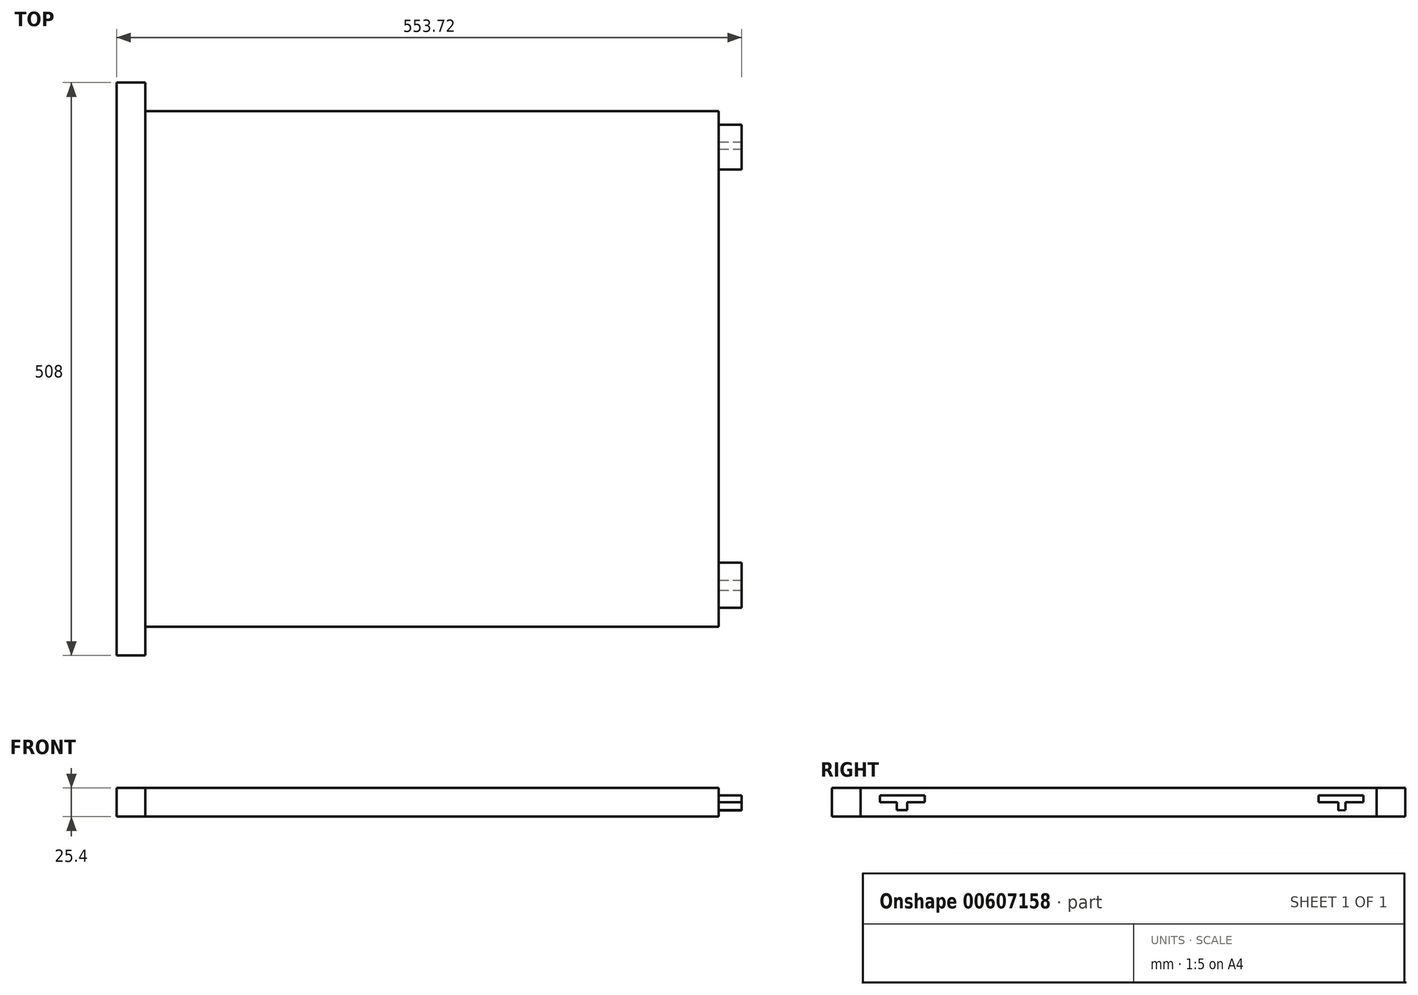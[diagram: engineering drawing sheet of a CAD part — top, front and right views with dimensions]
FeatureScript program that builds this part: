
annotation { "Feature Type Name" : "Feature", "Feature Type Description" : "" }
export const myFeature = defineFeature(function(context is Context, id is Id, definition is map)
    precondition{}
    {
        {
            var Q0;
            Q0=qCreatedBy(makeId("Top.planeOp"),FACE);
            var sketch = newSketch(context, id + "F0", { "sketchPlane" : qUnion([Q0])});
            skLineSegment(sketch, "E0.bottom", {"start": v(-230.83, 140.76) * mm, "end": v(277.17, 140.76) * mm});
            skLineSegment(sketch, "E0.top", {"start": v(-230.83, -316.44) * mm, "end": v(277.17, -316.44) * mm});
            skLineSegment(sketch, "E0.left", {"start": v(-230.83, 140.76) * mm, "end": v(-230.83, -316.44) * mm});
            skLineSegment(sketch, "E0.right", {"start": v(277.17, 140.76) * mm, "end": v(277.17, -316.44) * mm});
            skSolve(sketch);
        }
        {
            var Q0;
            Q0=makeQuery(id+"F0.imprint","IMPRINT",FACE,{"disambiguationData":[TD([[makeQuery(id+"F0.imprint","IMPRINT",EDGE,{"derivedFrom":sQuery(id+"F0.wireOp",EDGE,"E0.bottom")}),-1.0]])]});
            extrude(context, id + "F1", {"entities" : qUnion([Q0]), "depth" : 25.4 * mm, "offsetDistance" : 25.4 * mm});
        }
        {
            var Q0;
            Q0=makeQuery(id+"F1.opExtrude","CAP_FACE",FACE,{"disambiguationData":[OSD([sQuery(id+"F0.wireOp",EDGE,"E0.bottom"),sQuery(id+"F0.wireOp",EDGE,"E0.top"),sQuery(id+"F0.wireOp",EDGE,"E0.left"),sQuery(id+"F0.wireOp",EDGE,"E0.right")])],"isStart":true});
            var sketch = newSketch(context, id + "F2", { "sketchPlane" : qUnion([Q0])});
            skLineSegment(sketch, "E1.bottom", {"start": v(-230.83, 341.84) * mm, "end": v(-256.23, 341.84) * mm});
            skLineSegment(sketch, "E1.top", {"start": v(-230.83, -166.16) * mm, "end": v(-256.23, -166.16) * mm});
            skLineSegment(sketch, "E1.left", {"start": v(-230.83, 341.84) * mm, "end": v(-230.83, -166.16) * mm});
            skLineSegment(sketch, "E1.right", {"start": v(-256.23, 341.84) * mm, "end": v(-256.23, -166.16) * mm});
            skSolve(sketch);
        }
        {
            var Q0;
            {var subQ2=sQuery(id+"F2.wireOp",EDGE,"E1.bottom");Q0=makeQuery(id+"F2.imprint","IMPRINT",FACE,{"disambiguationData":[TD([[makeQuery(id+"F2.imprint","IMPRINT",EDGE,{"derivedFrom":subQ2}),1.0]])]});}
            var Q1;
            Q1=makeQuery(id+"F1.opExtrude","CAP_FACE",FACE,{"disambiguationData":[OSD([sQuery(id+"F0.wireOp",EDGE,"E0.bottom"),sQuery(id+"F0.wireOp",EDGE,"E0.top"),sQuery(id+"F0.wireOp",EDGE,"E0.left"),sQuery(id+"F0.wireOp",EDGE,"E0.right")])],"isStart":false});
            extrude(context, id + "F3", {"entities" : qUnion([Q0]), "endBound" : BoundingType.UP_TO_SURFACE, "oppositeDirection" : true, "depth" : 76.2 * mm, "endBoundEntityFace" : qUnion([Q1]), "offsetDistance" : 25.4 * mm});
        }
        {
            var Q0;
            Q0=makeQuery(id+"F1.opExtrude","SWEPT_FACE",FACE,{"disambiguationData":[OSD([sQuery(id+"F0.wireOp",EDGE,"E0.right")])]});
            var sketch = newSketch(context, id + "F4", { "sketchPlane" : qUnion([Q0])});
            skLineSegment(sketch, "E2", {"start": v(-299.37, 18.83) * mm, "end": v(-259.63, 18.83) * mm});
            skLineSegment(sketch, "E3", {"start": v(-299.37, 18.83) * mm, "end": v(-299.37, 12.7) * mm});
            skPoint(sketch, "E3.endSnap0", {"position": v(-316.44, 12.7) * mm});
            skLineSegment(sketch, "E4", {"start": v(-299.37, 12.7) * mm, "end": v(-284.2, 12.7) * mm});
            skLineSegment(sketch, "E5", {"start": v(-284.2, 12.7) * mm, "end": v(-284.2, 5.75) * mm});
            skLineSegment(sketch, "E6", {"start": v(-284.2, 5.75) * mm, "end": v(-275.31, 5.75) * mm});
            skLineSegment(sketch, "E7", {"start": v(-275.31, 5.75) * mm, "end": v(-275.31, 12.7) * mm});
            skLineSegment(sketch, "E8", {"start": v(-275.31, 12.7) * mm, "end": v(-259.63, 12.7) * mm});
            skLineSegment(sketch, "E9", {"start": v(-259.63, 12.7) * mm, "end": v(-259.63, 18.83) * mm});
            skLineSegment(sketch, "E10", {"start": v(89.18, 12.7) * mm, "end": v(89.18, 18.83) * mm});
            skLineSegment(sketch, "E11", {"start": v(89.18, 18.83) * mm, "end": v(128.92, 18.83) * mm});
            skLineSegment(sketch, "E12", {"start": v(128.92, 18.83) * mm, "end": v(128.92, 12.7) * mm});
            skLineSegment(sketch, "E13", {"start": v(128.92, 12.7) * mm, "end": v(113.23, 12.7) * mm});
            skLineSegment(sketch, "E14", {"start": v(113.23, 12.7) * mm, "end": v(113.23, 5.75) * mm});
            skLineSegment(sketch, "E15", {"start": v(89.18, 12.7) * mm, "end": v(106.75, 12.7) * mm});
            skLineSegment(sketch, "E16", {"start": v(106.75, 12.7) * mm, "end": v(106.75, 5.47) * mm});
            skLineSegment(sketch, "E17", {"start": v(106.75, 5.47) * mm, "end": v(113.23, 5.75) * mm});
            skSolve(sketch);
        }
        {
            var Q0;
            Q0 = qSketchRegion(id + "F4", true);
            extrude(context, id + "F5", {"entities" : qUnion([Q0]), "operationType" : NewBodyOperationType.ADD, "depth" : 20.32 * mm, "offsetDistance" : 25.4 * mm});
        }
    });
